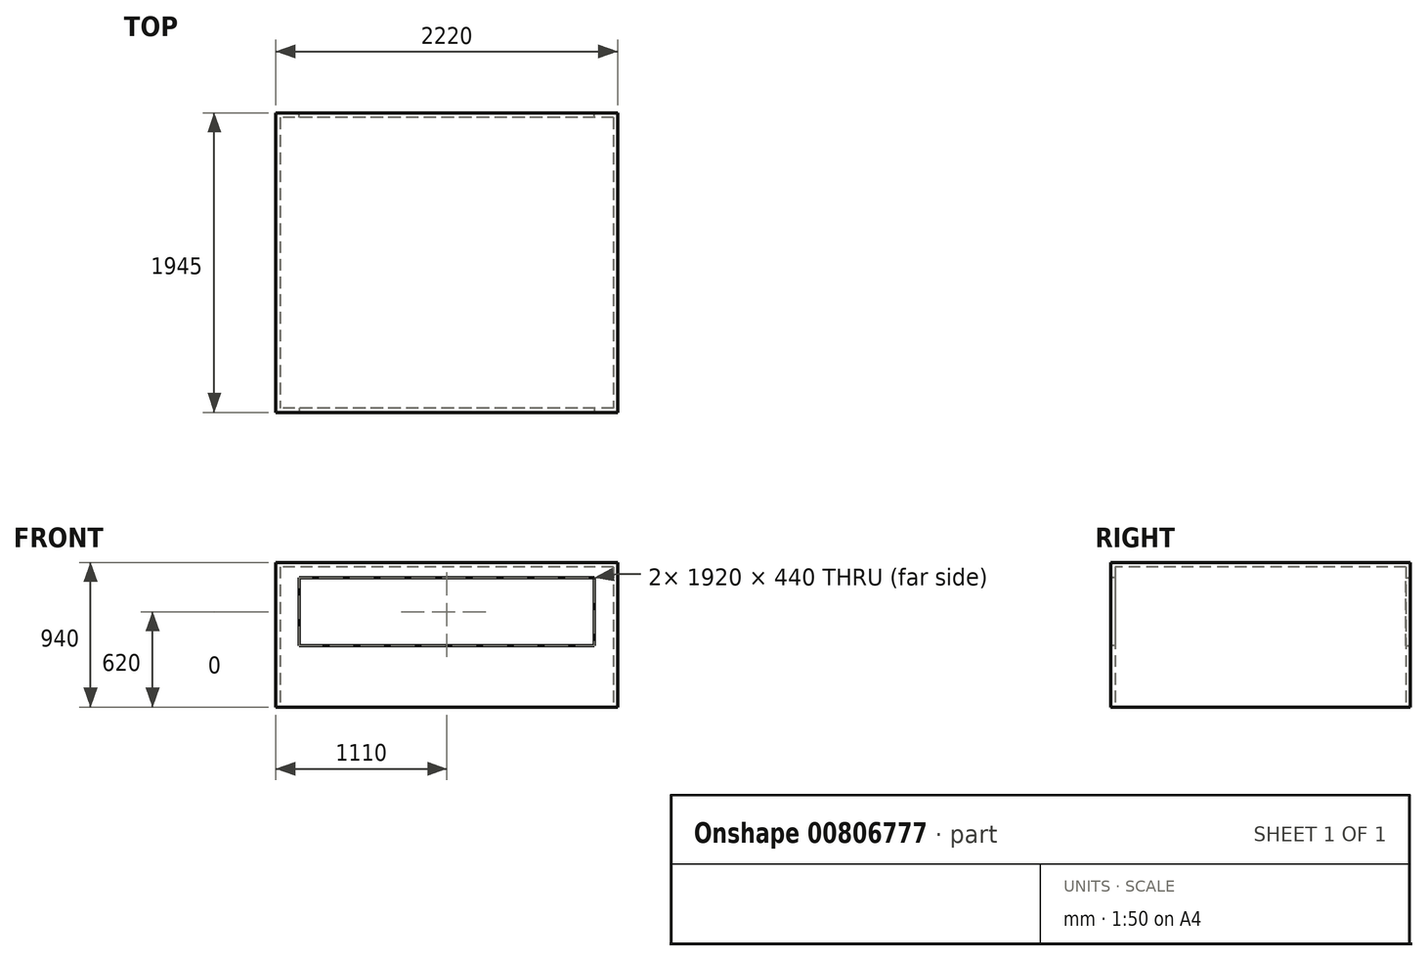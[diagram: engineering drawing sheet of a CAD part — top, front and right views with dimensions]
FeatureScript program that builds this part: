
annotation { "Feature Type Name" : "Feature", "Feature Type Description" : "" }
export const myFeature = defineFeature(function(context is Context, id is Id, definition is map)
    precondition{}
    {
        {
            var Q0;
            Q0=qCreatedBy(makeId("Top.planeOp"),FACE);
            var sketch = newSketch(context, id + "F0", { "sketchPlane" : qUnion([Q0])});
            skLineSegment(sketch, "E0.bottom", {"start": v(1110, 972.5) * mm, "end": v(-1110, 972.5) * mm});
            skLineSegment(sketch, "E0.top", {"start": v(1110, -972.5) * mm, "end": v(-1110, -972.5) * mm});
            skLineSegment(sketch, "E0.left", {"start": v(1110, 972.5) * mm, "end": v(1110, -972.5) * mm});
            skLineSegment(sketch, "E0.right", {"start": v(-1110, 972.5) * mm, "end": v(-1110, -972.5) * mm});
            skPoint(sketch, "E0.middle", {"position": v(0, 0) * mm});
            skSolve(sketch);
        }
        {
            var Q0;
            Q0=makeQuery(id+"F0.imprint","IMPRINT",FACE,{"disambiguationData":[TD([[makeQuery(id+"F0.imprint","IMPRINT",EDGE,{"derivedFrom":sQuery(id+"F0.wireOp",EDGE,"E0.bottom")}),1.0]])]});
            extrude(context, id + "F1", {"entities" : qUnion([Q0]), "depth" : 940 * mm, "offsetDistance" : 25 * mm});
        }
        {
            var Q0;
            Q0=makeQuery(id+"F1.opExtrude","CAP_FACE",FACE,{"disambiguationData":[OSD([sQuery(id+"F0.wireOp",EDGE,"E0.bottom"),sQuery(id+"F0.wireOp",EDGE,"E0.top"),sQuery(id+"F0.wireOp",EDGE,"E0.left"),sQuery(id+"F0.wireOp",EDGE,"E0.right")])],"isStart":true});
            shell(context, id + "F2", {"entities" : qUnion([Q0]), "thickness" : 28.5 * mm});
        }
        {
            var Q0;
            Q0=makeQuery(id+"F1.opExtrude","SWEPT_FACE",FACE,{"disambiguationData":[OSD([sQuery(id+"F0.wireOp",EDGE,"E0.top")])]});
            var sketch = newSketch(context, id + "F3", { "sketchPlane" : qUnion([Q0])});
            skLineSegment(sketch, "E1.bottom", {"start": v(-960, 400) * mm, "end": v(960, 400) * mm});
            skLineSegment(sketch, "E1.top", {"start": v(-960, 840) * mm, "end": v(960, 840) * mm});
            skLineSegment(sketch, "E1.left", {"start": v(-960, 400) * mm, "end": v(-960, 840) * mm});
            skLineSegment(sketch, "E1.right", {"start": v(960, 400) * mm, "end": v(960, 840) * mm});
            skSolve(sketch);
        }
        {
            var Q0;
            Q0=makeQuery(id+"F3.imprint","IMPRINT",FACE,{"disambiguationData":[TD([[makeQuery(id+"F3.imprint","IMPRINT",EDGE,{"derivedFrom":sQuery(id+"F3.wireOp",EDGE,"E1.bottom")}),1.0]])]});
            extrude(context, id + "F4", {"entities" : qUnion([Q0]), "operationType" : NewBodyOperationType.REMOVE, "endBound" : BoundingType.UP_TO_NEXT, "oppositeDirection" : true, "depth" : 25 * mm, "offsetDistance" : 25 * mm});
        }
        {
            var Q0;
            Q0=makeQuery(id+"F1.opExtrude","SWEPT_FACE",FACE,{"disambiguationData":[OSD([sQuery(id+"F0.wireOp",EDGE,"E0.bottom")])]});
            var sketch = newSketch(context, id + "F5", { "sketchPlane" : qUnion([Q0])});
            skPoint(sketch, "E2.0", {"position": v(-960, 400) * mm});
            skPoint(sketch, "E3.0", {"position": v(960, 840) * mm});
            skLineSegment(sketch, "E4.bottom", {"start": v(-960, 400) * mm, "end": v(960, 400) * mm});
            skLineSegment(sketch, "E4.top", {"start": v(-960, 840) * mm, "end": v(960, 840) * mm});
            skLineSegment(sketch, "E4.left", {"start": v(-960, 400) * mm, "end": v(-960, 840) * mm});
            skLineSegment(sketch, "E4.right", {"start": v(960, 400) * mm, "end": v(960, 840) * mm});
            skSolve(sketch);
        }
        {
            var Q0;
            Q0=makeQuery(id+"F5.imprint","IMPRINT",FACE,{"disambiguationData":[TD([[makeQuery(id+"F5.imprint","IMPRINT",EDGE,{"derivedFrom":sQuery(id+"F5.wireOp",EDGE,"E4.bottom")}),1.0]])]});
            extrude(context, id + "F6", {"entities" : qUnion([Q0]), "operationType" : NewBodyOperationType.REMOVE, "endBound" : BoundingType.UP_TO_NEXT, "oppositeDirection" : true, "depth" : 25 * mm, "offsetDistance" : 25 * mm});
        }
    });
